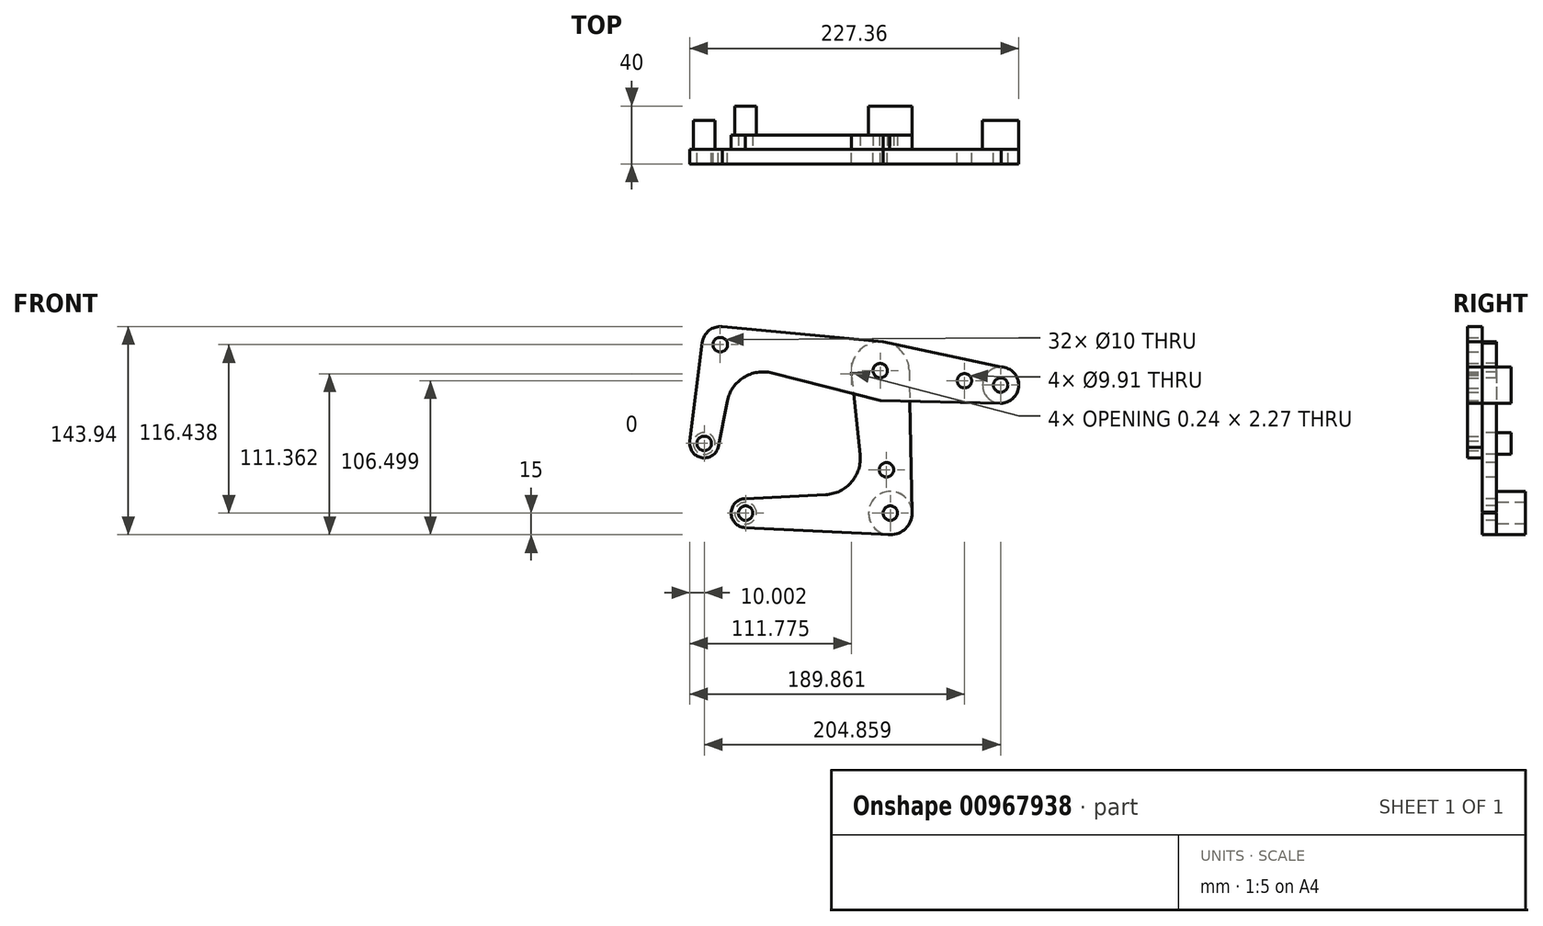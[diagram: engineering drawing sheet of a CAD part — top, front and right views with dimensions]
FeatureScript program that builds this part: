
annotation { "Feature Type Name" : "Feature", "Feature Type Description" : "" }
export const myFeature = defineFeature(function(context is Context, id is Id, definition is map)
    precondition{}
    {
        {
            var Q0;
            Q0=qCreatedBy(makeId("Front.planeOp"),FACE);
            var sketch = newSketch(context, id + "F0", { "sketchPlane" : qUnion([Q0])});
            skCircle(sketch, "E0", {"center": v(0, 0) * mm, "radius": 15 * mm});
            skLineSegment(sketch, "E1", {"start": v(0, 0) * mm, "end": v(-100, 0) * mm, "construction": true});
            skCircle(sketch, "E2", {"center": v(-100, 0) * mm, "radius": 10 * mm});
            skCircle(sketch, "E3", {"center": v(-6.98, 98.47) * mm, "radius": 20 * mm});
            skLineSegment(sketch, "E4", {"start": v(0, 0) * mm, "end": v(-8.75, 100) * mm, "construction": true});
            skLineSegment(sketch, "E5", {"start": v(13.02, 98.82) * mm, "end": v(15, 0) * mm});
            skLineSegment(sketch, "E6", {"start": v(-100.5, -9.99) * mm, "end": v(0, -15) * mm});
            skLineSegment(sketch, "E7", {"start": v(-100.28, 10) * mm, "end": v(-44.5, 12.78) * mm});
            skLineSegment(sketch, "E8", {"start": v(-26.96, 97.5) * mm, "end": v(-20.89, 40.4) * mm});
            skPoint(sketch, "E9", {"position": v(-18.1, 14.1) * mm});
            skLineSegment(sketch, "E10.trimOffspring", {"start": v(-1.3, 14.93) * mm, "end": v(0, 15) * mm});
            skArc(sketch, "E11.filletArc", {"start": v(-44.5, 12.78) * mm, "mid": v(-26.75, 21.5) * mm, "end": v(-20.89, 40.4) * mm});
            skCircle(sketch, "E12", {"center": v(-100, 0) * mm, "radius": 5 * mm});
            skCircle(sketch, "E13", {"center": v(0, 0) * mm, "radius": 5 * mm});
            skCircle(sketch, "E14", {"center": v(-6.98, 98.47) * mm, "radius": 5 * mm});
            skPoint(sketch, "E15", {"position": v(-2.62, 29.93) * mm});
            skCircle(sketch, "E16", {"center": v(-2.62, 29.93) * mm, "radius": 5 * mm});
            skLineSegment(sketch, "E17", {"start": v(-117.51, 116.44) * mm, "end": v(-6.98, 98.47) * mm, "construction": true});
            skLineSegment(sketch, "E18", {"start": v(-6.98, 98.47) * mm, "end": v(76.25, 88.5) * mm, "construction": true});
            skCircle(sketch, "E19", {"center": v(-117.51, 116.44) * mm, "radius": 12.5 * mm});
            skCircle(sketch, "E20", {"center": v(76.25, 88.5) * mm, "radius": 12.5 * mm});
            skLineSegment(sketch, "E21", {"start": v(-116.08, 128.86) * mm, "end": v(-5.1, 118.38) * mm});
            skLineSegment(sketch, "E22", {"start": v(-5.1, 118.38) * mm, "end": v(76.7, 101) * mm});
            skLineSegment(sketch, "E23", {"start": v(-81.88, 96.87) * mm, "end": v(-6.8, 77.8) * mm});
            skLineSegment(sketch, "E24", {"start": v(-6.8, 77.8) * mm, "end": v(75.98, 76) * mm});
            skLineSegment(sketch, "E25", {"start": v(-117.51, 116.44) * mm, "end": v(-128.6, 48.17) * mm, "construction": true});
            skCircle(sketch, "E26", {"center": v(-128.6, 48.17) * mm, "radius": 10 * mm});
            skLineSegment(sketch, "E27", {"start": v(-138.48, 49.78) * mm, "end": v(-129.92, 118) * mm});
            skLineSegment(sketch, "E28", {"start": v(-118.96, 45.55) * mm, "end": v(-112.55, 77.55) * mm});
            skPoint(sketch, "E29", {"position": v(-107.38, 103.36) * mm});
            skLineSegment(sketch, "E30.trimOffspring", {"start": v(-105.26, 113.98) * mm, "end": v(-105.17, 114.43) * mm});
            skArc(sketch, "E31.filletArc", {"start": v(-81.88, 96.87) * mm, "mid": v(-101.36, 93.8) * mm, "end": v(-112.55, 77.55) * mm});
            skCircle(sketch, "E32", {"center": v(-117.51, 116.44) * mm, "radius": 5 * mm});
            skCircle(sketch, "E33", {"center": v(-128.6, 48.17) * mm, "radius": 5 * mm});
            skCircle(sketch, "E34", {"center": v(76.25, 88.5) * mm, "radius": 5 * mm});
            skCircle(sketch, "E35", {"center": v(-128.6, 48.17) * mm, "radius": 7.5 * mm});
            skPoint(sketch, "E36", {"position": v(51.25, 91.5) * mm});
            skCircle(sketch, "E37", {"center": v(51.25, 91.5) * mm, "radius": 4.95 * mm});
            skSolve(sketch);
        }
        {
            var Q0;
            {var subQ0=sQuery(id+"F0.wireOp",EDGE,"E21");Q0=makeQuery(id+"F0.imprint","IMPRINT",FACE,{"disambiguationData":[TD([[makeQuery(id+"F0.imprint","IMPRINT",EDGE,{"derivedFrom":subQ0}),-1.0]])]});}
            var Q1;
            Q1=makeQuery(id+"F0.imprint","IMPRINT",FACE,{"disambiguationData":[TD([[makeQuery(id+"F0.imprint","IMPRINT",EDGE,{"derivedFrom":sQuery(id+"F0.wireOp",EDGE,"E14")}),-1.0]])]});
            var Q2;
            {var subQ0=sQuery(id+"F0.wireOp",EDGE,"E8");var subQ1=sQuery(id+"F0.wireOp",EDGE,"E3");var subQ2=makeQuery(id+"F0.imprint","INTERSECT",VERTEX,{"derivedFrom":[subQ1,subQ0]});Q2=makeQuery(id+"F0.imprint","IMPRINT",FACE,{"disambiguationData":[TD([[makeQuery(id+"F0.imprint","IMPRINT",EDGE,{"disambiguationData":[TD([[subQ2,-1.0]])],"derivedFrom":subQ1}),-1.0]])]});}
            var Q3;
            {var subQ0=sQuery(id+"F0.wireOp",EDGE,"E5");var subQ1=sQuery(id+"F0.wireOp",EDGE,"E3");var subQ2=makeQuery(id+"F0.imprint","INTERSECT",VERTEX,{"derivedFrom":[subQ1,subQ0]});Q3=makeQuery(id+"F0.imprint","IMPRINT",FACE,{"disambiguationData":[TD([[makeQuery(id+"F0.imprint","IMPRINT",EDGE,{"disambiguationData":[TD([[subQ2,1.0]])],"derivedFrom":subQ1}),-1.0]])]});}
            var Q4;
            {var subQ5=sQuery(id+"F0.wireOp",EDGE,"E3");var subQ7=sQuery(id+"F0.wireOp",EDGE,"E5");var subQ8=makeQuery(id+"F0.imprint","INTERSECT",VERTEX,{"derivedFrom":[subQ5,subQ7]});Q4=makeQuery(id+"F0.imprint","IMPRINT",FACE,{"disambiguationData":[TD([[makeQuery(id+"F0.imprint","IMPRINT",EDGE,{"disambiguationData":[TD([[subQ8,-1.0]])],"derivedFrom":subQ5}),-1.0]])]});}
            var Q5;
            Q5=makeQuery(id+"F0.imprint","IMPRINT",FACE,{"disambiguationData":[TD([[makeQuery(id+"F0.imprint","IMPRINT",EDGE,{"derivedFrom":sQuery(id+"F0.wireOp",EDGE,"E34")}),-1.0]])]});
            var Q6;
            Q6=makeQuery(id+"F0.imprint","IMPRINT",FACE,{"disambiguationData":[TD([[makeQuery(id+"F0.imprint","IMPRINT",EDGE,{"derivedFrom":sQuery(id+"F0.wireOp",EDGE,"E32")}),-1.0]])]});
            var Q7;
            Q7=makeQuery(id+"F0.imprint","IMPRINT",FACE,{"disambiguationData":[TD([[makeQuery(id+"F0.imprint","IMPRINT",EDGE,{"derivedFrom":sQuery(id+"F0.wireOp",EDGE,"E35")}),-1.0]])]});
            var Q8;
            Q8=makeQuery(id+"F0.imprint","IMPRINT",FACE,{"disambiguationData":[TD([[makeQuery(id+"F0.imprint","IMPRINT",EDGE,{"derivedFrom":sQuery(id+"F0.wireOp",EDGE,"E33")}),-1.0]])]});
            extrude(context, id + "F1", {"entities" : qUnion([Q0, Q1, Q2, Q3, Q4, Q5, Q6, Q7, Q8]), "depth" : 10 * mm, "offsetDistance" : 25 * mm});
        }
        {
            var Q0;
            {var subQ13=sQuery(id+"F0.wireOp",EDGE,"E7");Q0=makeQuery(id+"F0.imprint","IMPRINT",FACE,{"disambiguationData":[TD([[makeQuery(id+"F0.imprint","IMPRINT",EDGE,{"derivedFrom":subQ13}),-1.0]])]});}
            var Q1;
            Q1=makeQuery(id+"F0.imprint","IMPRINT",FACE,{"disambiguationData":[TD([[makeQuery(id+"F0.imprint","IMPRINT",EDGE,{"derivedFrom":sQuery(id+"F0.wireOp",EDGE,"E14")}),-1.0]])]});
            var Q2;
            {var subQ0=sQuery(id+"F0.wireOp",EDGE,"E5");var subQ1=sQuery(id+"F0.wireOp",EDGE,"E3");var subQ2=makeQuery(id+"F0.imprint","INTERSECT",VERTEX,{"derivedFrom":[subQ1,subQ0]});Q2=makeQuery(id+"F0.imprint","IMPRINT",FACE,{"disambiguationData":[TD([[makeQuery(id+"F0.imprint","IMPRINT",EDGE,{"disambiguationData":[TD([[subQ2,1.0]])],"derivedFrom":subQ1}),-1.0]])]});}
            var Q3;
            {var subQ0=sQuery(id+"F0.wireOp",EDGE,"E8");var subQ1=sQuery(id+"F0.wireOp",EDGE,"E3");var subQ2=makeQuery(id+"F0.imprint","INTERSECT",VERTEX,{"derivedFrom":[subQ1,subQ0]});Q3=makeQuery(id+"F0.imprint","IMPRINT",FACE,{"disambiguationData":[TD([[makeQuery(id+"F0.imprint","IMPRINT",EDGE,{"disambiguationData":[TD([[subQ2,-1.0]])],"derivedFrom":subQ1}),-1.0]])]});}
            var Q4;
            Q4=makeQuery(id+"F0.imprint","IMPRINT",FACE,{"disambiguationData":[TD([[makeQuery(id+"F0.imprint","IMPRINT",EDGE,{"derivedFrom":sQuery(id+"F0.wireOp",EDGE,"E13")}),-1.0]])]});
            var Q5;
            Q5=makeQuery(id+"F0.imprint","IMPRINT",FACE,{"disambiguationData":[TD([[makeQuery(id+"F0.imprint","IMPRINT",EDGE,{"derivedFrom":sQuery(id+"F0.wireOp",EDGE,"E12")}),-1.0]])]});
            extrude(context, id + "F2", {"entities" : qUnion([Q0, Q1, Q2, Q3, Q4, Q5]), "oppositeDirection" : true, "depth" : 10 * mm, "offsetDistance" : 25 * mm});
        }
        {
            var Q0;
            Q0=makeQuery(id+"F1.opExtrude","CAP_FACE",FACE,{"disambiguationData":[OSD([sQuery(id+"F0.wireOp",EDGE,"E3"),sQuery(id+"F0.wireOp",EDGE,"E8"),sQuery(id+"F0.wireOp",EDGE,"E14"),sQuery(id+"F0.wireOp",EDGE,"E19"),sQuery(id+"F0.wireOp",EDGE,"E20"),sQuery(id+"F0.wireOp",EDGE,"E21"),sQuery(id+"F0.wireOp",EDGE,"E22"),sQuery(id+"F0.wireOp",EDGE,"E23"),sQuery(id+"F0.wireOp",EDGE,"E24"),sQuery(id+"F0.wireOp",EDGE,"E26"),sQuery(id+"F0.wireOp",EDGE,"E27"),sQuery(id+"F0.wireOp",EDGE,"E28"),sQuery(id+"F0.wireOp",EDGE,"E31.filletArc"),sQuery(id+"F0.wireOp",EDGE,"E32"),sQuery(id+"F0.wireOp",EDGE,"E33"),sQuery(id+"F0.wireOp",EDGE,"E34"),sQuery(id+"F0.wireOp",EDGE,"E37")])],"isStart":false});
            var sketch = newSketch(context, id + "F3", { "sketchPlane" : qUnion([Q0])});
            skCircle(sketch, "E38.0", {"center": v(76.25, 88.5) * mm, "radius": 12.5 * mm});
            skCircle(sketch, "E39.0", {"center": v(-128.6, 48.17) * mm, "radius": 7.5 * mm});
            skSolve(sketch);
        }
        {
            var Q0;
            {var subQ4=sQuery(id+"F0.wireOp",EDGE,"E7");Q0=makeQuery(id+"F0.imprint","IMPRINT",FACE,{"disambiguationData":[TD([[makeQuery(id+"F0.imprint","IMPRINT",EDGE,{"derivedFrom":subQ4}),-1.0]])]});}
            var sketch = newSketch(context, id + "F4", { "sketchPlane" : qUnion([Q0])});
            skCircle(sketch, "E40.0", {"center": v(0, 0) * mm, "radius": 15 * mm});
            skPoint(sketch, "E41.0", {"position": v(-100, 0) * mm});
            skCircle(sketch, "E42", {"center": v(-100, 0) * mm, "radius": 7.5 * mm});
            skSolve(sketch);
        }
        {
            var Q0;
            Q0 = qSketchRegion(id + "F4", true);
            var Q1;
            Q1 = qSketchRegion(id + "F3", true);
            extrude(context, id + "F5", {"entities" : qUnion([Q0, Q1]), "oppositeDirection" : true, "depth" : 30 * mm, "offsetDistance" : 25 * mm});
        }
        {
            var Q0;
            Q0=makeQuery(id+"F1.opExtrude","SWEPT_BODY",BODY,{"disambiguationData":[OSD([sQuery(id+"F0.wireOp",EDGE,"E3"),sQuery(id+"F0.wireOp",EDGE,"E8"),sQuery(id+"F0.wireOp",EDGE,"E14"),sQuery(id+"F0.wireOp",EDGE,"E19"),sQuery(id+"F0.wireOp",EDGE,"E20"),sQuery(id+"F0.wireOp",EDGE,"E21"),sQuery(id+"F0.wireOp",EDGE,"E22"),sQuery(id+"F0.wireOp",EDGE,"E23"),sQuery(id+"F0.wireOp",EDGE,"E24"),sQuery(id+"F0.wireOp",EDGE,"E26"),sQuery(id+"F0.wireOp",EDGE,"E27"),sQuery(id+"F0.wireOp",EDGE,"E28"),sQuery(id+"F0.wireOp",EDGE,"E31.filletArc"),sQuery(id+"F0.wireOp",EDGE,"E32"),sQuery(id+"F0.wireOp",EDGE,"E33"),sQuery(id+"F0.wireOp",EDGE,"E34"),sQuery(id+"F0.wireOp",EDGE,"E37")])]});
            var Q1;
            Q1=makeQuery(id+"F2.opExtrude","SWEPT_BODY",BODY,{"disambiguationData":[OSD([sQuery(id+"F0.wireOp",EDGE,"E0"),sQuery(id+"F0.wireOp",EDGE,"E2"),sQuery(id+"F0.wireOp",EDGE,"E3"),sQuery(id+"F0.wireOp",EDGE,"E5"),sQuery(id+"F0.wireOp",EDGE,"E6"),sQuery(id+"F0.wireOp",EDGE,"E7"),sQuery(id+"F0.wireOp",EDGE,"E8"),sQuery(id+"F0.wireOp",EDGE,"E11.filletArc"),sQuery(id+"F0.wireOp",EDGE,"E12"),sQuery(id+"F0.wireOp",EDGE,"E13"),sQuery(id+"F0.wireOp",EDGE,"E14"),sQuery(id+"F0.wireOp",EDGE,"E16"),sQuery(id+"F0.wireOp",EDGE,"E22")])]});
            var Q2;
            Q2=makeQuery(id+"F5.opExtrude","SWEPT_BODY",BODY,{"disambiguationData":[OSD([sQuery(id+"F3.wireOp",EDGE,"E38.0")])]});
            var Q3;
            Q3=makeQuery(id+"F5.opExtrude","SWEPT_BODY",BODY,{"disambiguationData":[OSD([sQuery(id+"F4.wireOp",EDGE,"E40.0")])]});
            var Q4;
            Q4=makeQuery(id+"F5.opExtrude","SWEPT_BODY",BODY,{"disambiguationData":[OSD([sQuery(id+"F4.wireOp",EDGE,"E42")])]});
            var Q5;
            Q5=makeQuery(id+"F5.opExtrude","SWEPT_BODY",BODY,{"disambiguationData":[OSD([sQuery(id+"F3.wireOp",EDGE,"E39.0")])]});
            booleanBodies(context, id + "F6", {"operationType" : BooleanOperationType.SUBTRACTION, "tools" : qUnion([Q0, Q1]), "targets" : qUnion([Q2, Q3, Q4, Q5]), "keepTools" : true});
        }
    });
